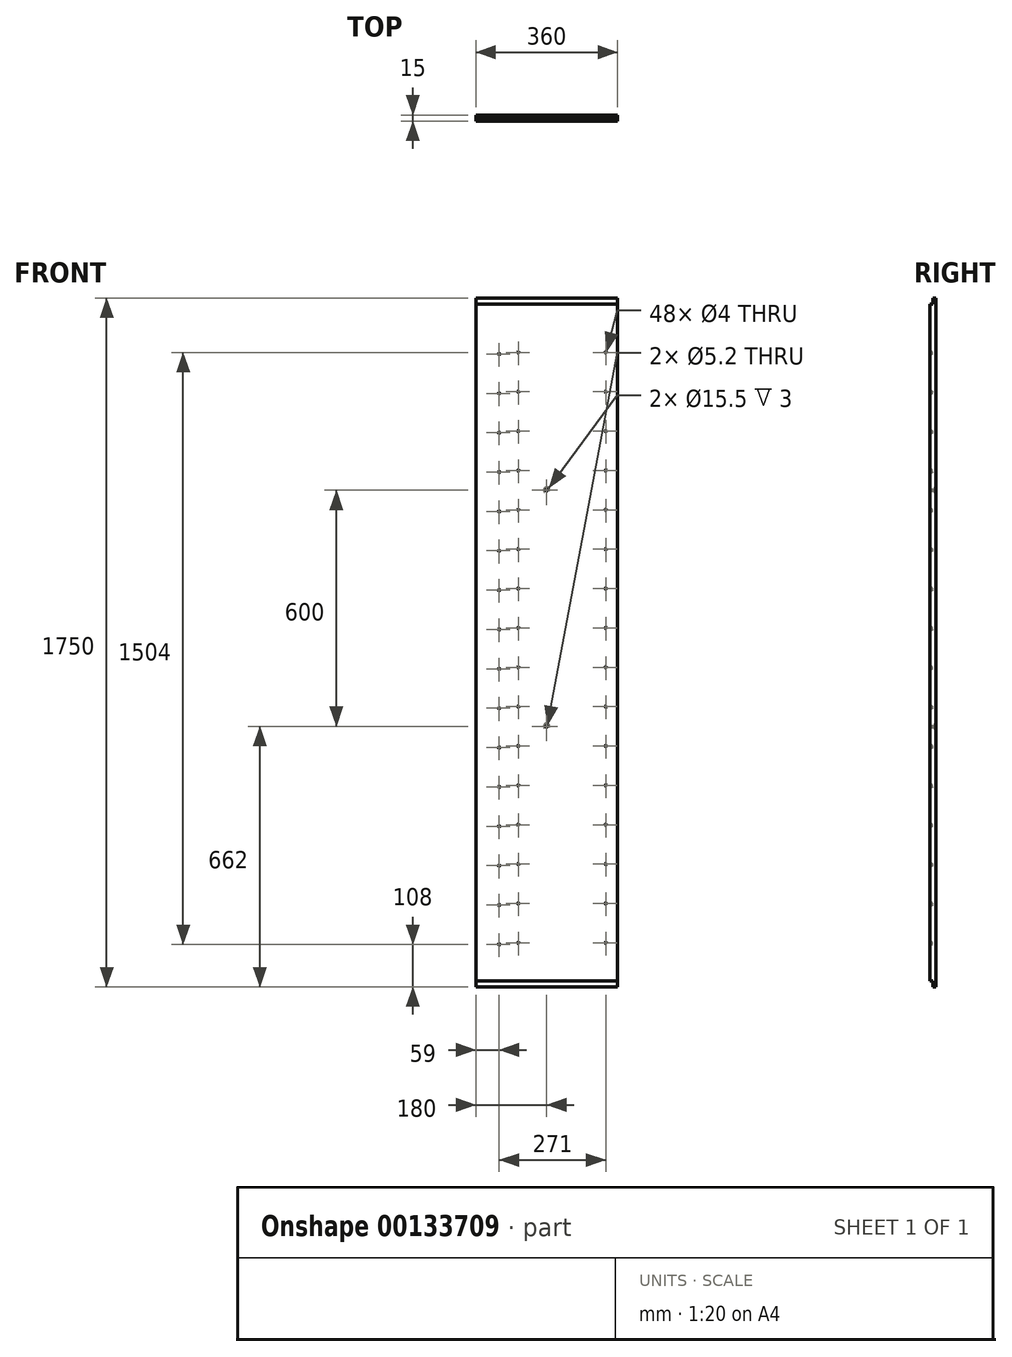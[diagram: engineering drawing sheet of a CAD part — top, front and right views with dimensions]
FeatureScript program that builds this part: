
annotation { "Feature Type Name" : "Feature", "Feature Type Description" : "" }
export const myFeature = defineFeature(function(context is Context, id is Id, definition is map)
    precondition{}
    {
        {
            var Q0;
            Q0=qCreatedBy(makeId("Front.planeOp"),FACE);
            var sketch = newSketch(context, id + "F0", { "sketchPlane" : qUnion([Q0])});
            skLineSegment(sketch, "E0.bottom", {"start": v(0, 0) * mm, "end": v(360, 0) * mm});
            skLineSegment(sketch, "E0.top", {"start": v(0, 1750) * mm, "end": v(360, 1750) * mm});
            skLineSegment(sketch, "E0.left", {"start": v(0, 0) * mm, "end": v(0, 1750) * mm});
            skLineSegment(sketch, "E0.right", {"start": v(360, 0) * mm, "end": v(360, 1750) * mm});
            skSolve(sketch);
        }
        {
            var Q0;
            Q0=makeQuery(id+"F0.imprint","IMPRINT",FACE,{"disambiguationData":[TD([[makeQuery(id+"F0.imprint","IMPRINT",EDGE,{"derivedFrom":sQuery(id+"F0.wireOp",EDGE,"E0.bottom")}),1.0]])]});
            extrude(context, id + "F1", {"entities" : qUnion([Q0]), "depth" : 15 * mm, "offsetDistance" : 25 * mm});
        }
        {
            var Q0;
            Q0=makeQuery(id+"F1.opExtrude","CAP_FACE",FACE,{"disambiguationData":[OSD([sQuery(id+"F0.wireOp",EDGE,"E0.bottom"),sQuery(id+"F0.wireOp",EDGE,"E0.top"),sQuery(id+"F0.wireOp",EDGE,"E0.left"),sQuery(id+"F0.wireOp",EDGE,"E0.right")])],"isStart":false});
            var sketch = newSketch(context, id + "F2", { "sketchPlane" : qUnion([Q0])});
            skPoint(sketch, "E1", {"position": v(330, 112) * mm});
            skPoint(sketch, "E2", {"position": v(108, 112) * mm});
            skPoint(sketch, "E3", {"position": v(59, 108) * mm});
            skPoint(sketch, "E4.0.1.0", {"position": v(59, 208) * mm});
            skPoint(sketch, "E4.0.1.1", {"position": v(108, 212) * mm});
            skPoint(sketch, "E4.0.1.2", {"position": v(330, 212) * mm});
            skPoint(sketch, "E4.0.2.0", {"position": v(59, 308) * mm});
            skPoint(sketch, "E4.0.2.1", {"position": v(108, 312) * mm});
            skPoint(sketch, "E4.0.2.2", {"position": v(330, 312) * mm});
            skPoint(sketch, "E4.0.3.0", {"position": v(59, 408) * mm});
            skPoint(sketch, "E4.0.3.1", {"position": v(108, 412) * mm});
            skPoint(sketch, "E4.0.3.2", {"position": v(330, 412) * mm});
            skPoint(sketch, "E4.0.4.0", {"position": v(59, 508) * mm});
            skPoint(sketch, "E4.0.4.1", {"position": v(108, 512) * mm});
            skPoint(sketch, "E4.0.4.2", {"position": v(330, 512) * mm});
            skPoint(sketch, "E4.0.5.0", {"position": v(59, 608) * mm});
            skPoint(sketch, "E4.0.5.1", {"position": v(108, 612) * mm});
            skPoint(sketch, "E4.0.5.2", {"position": v(330, 612) * mm});
            skPoint(sketch, "E4.0.6.0", {"position": v(59, 708) * mm});
            skPoint(sketch, "E4.0.6.1", {"position": v(108, 712) * mm});
            skPoint(sketch, "E4.0.6.2", {"position": v(330, 712) * mm});
            skPoint(sketch, "E4.0.7.0", {"position": v(59, 808) * mm});
            skPoint(sketch, "E4.0.7.1", {"position": v(108, 812) * mm});
            skPoint(sketch, "E4.0.7.2", {"position": v(330, 812) * mm});
            skPoint(sketch, "E4.0.8.0", {"position": v(59, 908) * mm});
            skPoint(sketch, "E4.0.8.1", {"position": v(108, 912) * mm});
            skPoint(sketch, "E4.0.8.2", {"position": v(330, 912) * mm});
            skPoint(sketch, "E4.0.9.0", {"position": v(59, 1008) * mm});
            skPoint(sketch, "E4.0.9.1", {"position": v(108, 1012) * mm});
            skPoint(sketch, "E4.0.9.2", {"position": v(330, 1012) * mm});
            skPoint(sketch, "E4.0.10.0", {"position": v(59, 1108) * mm});
            skPoint(sketch, "E4.0.10.1", {"position": v(108, 1112) * mm});
            skPoint(sketch, "E4.0.10.2", {"position": v(330, 1112) * mm});
            skPoint(sketch, "E4.0.11.0", {"position": v(59, 1208) * mm});
            skPoint(sketch, "E4.0.11.1", {"position": v(108, 1212) * mm});
            skPoint(sketch, "E4.0.11.2", {"position": v(330, 1212) * mm});
            skPoint(sketch, "E4.0.12.0", {"position": v(59, 1308) * mm});
            skPoint(sketch, "E4.0.12.1", {"position": v(108, 1312) * mm});
            skPoint(sketch, "E4.0.12.2", {"position": v(330, 1312) * mm});
            skPoint(sketch, "E4.0.13.0", {"position": v(59, 1408) * mm});
            skPoint(sketch, "E4.0.13.1", {"position": v(108, 1412) * mm});
            skPoint(sketch, "E4.0.13.2", {"position": v(330, 1412) * mm});
            skPoint(sketch, "E4.0.14.0", {"position": v(59, 1508) * mm});
            skPoint(sketch, "E4.0.14.1", {"position": v(108, 1512) * mm});
            skPoint(sketch, "E4.0.14.2", {"position": v(330, 1512) * mm});
            skPoint(sketch, "E4.0.15.0", {"position": v(59, 1608) * mm});
            skPoint(sketch, "E4.0.15.1", {"position": v(108, 1612) * mm});
            skPoint(sketch, "E4.0.15.2", {"position": v(330, 1612) * mm});
            skLineSegment(sketch, "E4.direction2", {"start": v(59, 108) * mm, "end": v(59, 208) * mm, "construction": true});
            skSolve(sketch);
        }
        {
            var Q0;
            Q0=sQuery(id+"F2.wireOp",VERTEX,"E4.0.12.0");
            var Q1;
            Q1=sQuery(id+"F2.wireOp",VERTEX,"E4.0.7.1");
            var Q2;
            Q2=sQuery(id+"F2.wireOp",VERTEX,"E4.0.12.2");
            var Q3;
            Q3=sQuery(id+"F2.wireOp",VERTEX,"E4.0.8.0");
            var Q4;
            Q4=sQuery(id+"F2.wireOp",VERTEX,"E4.0.13.2");
            var Q5;
            Q5=sQuery(id+"F2.wireOp",VERTEX,"E4.0.13.1");
            var Q6;
            Q6=sQuery(id+"F2.wireOp",VERTEX,"E4.0.9.0");
            var Q7;
            Q7=sQuery(id+"F2.wireOp",VERTEX,"E4.0.5.1");
            var Q8;
            Q8=sQuery(id+"F2.wireOp",VERTEX,"E4.0.5.0");
            var Q9;
            Q9=sQuery(id+"F2.wireOp",VERTEX,"E4.0.1.0");
            var Q10;
            Q10=sQuery(id+"F2.wireOp",VERTEX,"E4.0.2.0");
            var Q11;
            Q11=sQuery(id+"F2.wireOp",VERTEX,"E4.0.3.0");
            var Q12;
            Q12=sQuery(id+"F2.wireOp",VERTEX,"E4.0.14.2");
            var Q13;
            Q13=sQuery(id+"F2.wireOp",VERTEX,"E4.0.11.2");
            var Q14;
            Q14=sQuery(id+"F2.wireOp",VERTEX,"E4.0.7.0");
            var Q15;
            Q15=sQuery(id+"F2.wireOp",VERTEX,"E4.0.11.1");
            var Q16;
            Q16=sQuery(id+"F2.wireOp",VERTEX,"E4.0.15.2");
            var Q17;
            Q17=sQuery(id+"F2.wireOp",VERTEX,"E4.0.14.1");
            var Q18;
            Q18=sQuery(id+"F2.wireOp",VERTEX,"E4.0.10.1");
            var Q19;
            Q19=sQuery(id+"F2.wireOp",VERTEX,"E4.0.2.2");
            var Q20;
            Q20=sQuery(id+"F2.wireOp",VERTEX,"E4.0.2.1");
            var Q21;
            Q21=sQuery(id+"F2.wireOp",VERTEX,"E4.0.1.1");
            var Q22;
            Q22=sQuery(id+"F2.wireOp",VERTEX,"E4.0.4.1");
            var Q23;
            Q23=sQuery(id+"F2.wireOp",VERTEX,"E4.0.6.1");
            var Q24;
            Q24=sQuery(id+"F2.wireOp",VERTEX,"E4.0.5.2");
            var Q25;
            Q25=sQuery(id+"F2.wireOp",VERTEX,"E4.0.14.0");
            var Q26;
            Q26=sQuery(id+"F2.wireOp",VERTEX,"E4.0.12.1");
            var Q27;
            Q27=sQuery(id+"F2.wireOp",VERTEX,"E4.0.8.2");
            var Q28;
            Q28=sQuery(id+"F2.wireOp",VERTEX,"E4.0.15.0");
            var Q29;
            Q29=sQuery(id+"F2.wireOp",VERTEX,"E4.0.7.2");
            var Q30;
            Q30=sQuery(id+"F2.wireOp",VERTEX,"E4.0.9.2");
            var Q31;
            Q31=sQuery(id+"F2.wireOp",VERTEX,"E4.0.13.0");
            var Q32;
            Q32=sQuery(id+"F2.wireOp",VERTEX,"E4.0.1.2");
            var Q33;
            Q33=sQuery(id+"F2.wireOp",VERTEX,"E4.0.9.1");
            var Q34;
            Q34=sQuery(id+"F2.wireOp",VERTEX,"E4.direction1.end");
            var Q35;
            Q35=sQuery(id+"F2.wireOp",VERTEX,"E4.0.6.2");
            var Q36;
            Q36=sQuery(id+"F2.wireOp",VERTEX,"E2");
            var Q37;
            Q37=sQuery(id+"F2.wireOp",VERTEX,"E1");
            var Q38;
            Q38=sQuery(id+"F2.wireOp",VERTEX,"E4.0.4.2");
            var Q39;
            Q39=sQuery(id+"F2.wireOp",VERTEX,"E4.0.4.0");
            var Q40;
            Q40=sQuery(id+"F2.wireOp",VERTEX,"E3");
            var Q41;
            Q41=sQuery(id+"F2.wireOp",VERTEX,"E4.0.10.0");
            var Q42;
            Q42=sQuery(id+"F2.wireOp",VERTEX,"E4.0.15.1");
            var Q43;
            Q43=sQuery(id+"F2.wireOp",VERTEX,"E4.0.11.0");
            var Q44;
            Q44=sQuery(id+"F2.wireOp",VERTEX,"E4.0.6.0");
            var Q45;
            Q45=sQuery(id+"F2.wireOp",VERTEX,"E4.0.3.2");
            var Q46;
            Q46=sQuery(id+"F2.wireOp",VERTEX,"E4.0.3.1");
            var Q47;
            Q47=sQuery(id+"F2.wireOp",VERTEX,"E4.0.8.1");
            var Q48;
            Q48=sQuery(id+"F2.wireOp",VERTEX,"E4.0.10.2");
            var Q49;
            Q49=makeQuery(id+"F1.opExtrude","SWEPT_BODY",BODY,{"disambiguationData":[OSD([sQuery(id+"F0.wireOp",EDGE,"E0.bottom"),sQuery(id+"F0.wireOp",EDGE,"E0.top"),sQuery(id+"F0.wireOp",EDGE,"E0.left"),sQuery(id+"F0.wireOp",EDGE,"E0.right")])]});
            hole(context, id + "F3", {"style" : HoleStyle.SIMPLE, "endStyle" : HoleEndStyle.BLIND, "holeDiameter" : 4 * mm, "holeDepth" : 5 * mm, "isTappedThrough" : true, "tappedDepth" : 12 * mm, "tapClearance" : 3, "startFromSketch" : true, "locations" : qUnion([Q0, Q1, Q2, Q3, Q4, Q5, Q6, Q7, Q8, Q9, Q10, Q11, Q12, Q13, Q14, Q15, Q16, Q17, Q18, Q19, Q20, Q21, Q22, Q23, Q24, Q25, Q26, Q27, Q28, Q29, Q30, Q31, Q32, Q33, Q34, Q35, Q36, Q37, Q38, Q39, Q40, Q41, Q42, Q43, Q44, Q45, Q46, Q47, Q48]), "scope" : qUnion([Q49])});
        }
        {
            var Q0;
            Q0=makeQuery(id+"F1.opExtrude","CAP_FACE",FACE,{"disambiguationData":[OSD([sQuery(id+"F0.wireOp",EDGE,"E0.bottom"),sQuery(id+"F0.wireOp",EDGE,"E0.top"),sQuery(id+"F0.wireOp",EDGE,"E0.left"),sQuery(id+"F0.wireOp",EDGE,"E0.right")])],"isStart":true});
            var sketch = newSketch(context, id + "F4", { "sketchPlane" : qUnion([Q0])});
            skPoint(sketch, "E5.positionSnap0", {"position": v(-180, 0) * mm});
            skPoint(sketch, "E6", {"position": v(-180, 662) * mm});
            skPoint(sketch, "E7", {"position": v(-180, 1262) * mm});
            skSolve(sketch);
        }
        {
            var Q0;
            Q0=sQuery(id+"F4.wireOp",VERTEX,"E7");
            var Q1;
            Q1=sQuery(id+"F4.wireOp",VERTEX,"E6");
            var Q2;
            Q2=makeQuery(id+"F1.opExtrude","SWEPT_BODY",BODY,{"disambiguationData":[OSD([sQuery(id+"F0.wireOp",EDGE,"E0.bottom"),sQuery(id+"F0.wireOp",EDGE,"E0.top"),sQuery(id+"F0.wireOp",EDGE,"E0.left"),sQuery(id+"F0.wireOp",EDGE,"E0.right")])]});
            hole(context, id + "F5", {"style" : HoleStyle.C_BORE, "endStyle" : HoleEndStyle.BLIND, "holeDiameter" : 5.2 * mm, "cBoreDiameter" : 15.5 * mm, "cBoreDepth" : 3 * mm, "holeDepth" : 15 * mm, "isTappedThrough" : true, "tappedDepth" : 12 * mm, "tapClearance" : 3, "startFromSketch" : true, "locations" : qUnion([Q0, Q1]), "scope" : qUnion([Q2])});
        }
        {
            var Q0;
            Q0=makeQuery(id+"F1.opExtrude","SWEPT_FACE",FACE,{"disambiguationData":[OSD([sQuery(id+"F0.wireOp",EDGE,"E0.left")])]});
            var sketch = newSketch(context, id + "F6", { "sketchPlane" : qUnion([Q0])});
            skText(sketch, "E8", { "text": "123", "fontName": "OpenSans-Regular.ttf"});
            const initialGuessF6  = {"E8": [0, 0.8875, 1, 0, 0.00627]};
            skSetInitialGuess(sketch, initialGuessF6);
            skSolve(sketch);
        }
        {
            var Q0;
            Q0=makeQuery(id+"F6.imprint","IMPRINT",FACE,{"disambiguationData":[TD([[makeQuery(id+"F6.imprint","IMPRINT",EDGE,{"derivedFrom":sQuery(id+"F6.wireOp",EDGE,"E8.sketch_text.stroke-0")}),1.0]])]});
            var sketch = newSketch(context, id + "F7", { "sketchPlane" : qUnion([Q0])});
            skPoint(sketch, "E9.0", {"position": v(15, 0) * mm});
            skLineSegment(sketch, "E10.bottom", {"start": v(15, 0) * mm, "end": v(7.5, 0) * mm});
            skLineSegment(sketch, "E10.top", {"start": v(15, 15) * mm, "end": v(7.5, 15) * mm});
            skLineSegment(sketch, "E10.left", {"start": v(15, 0) * mm, "end": v(15, 15) * mm});
            skLineSegment(sketch, "E10.right", {"start": v(7.5, 0) * mm, "end": v(7.5, 15) * mm});
            skPoint(sketch, "E11.0", {"position": v(15, 1750) * mm});
            skLineSegment(sketch, "E12.bottom", {"start": v(15, 1750) * mm, "end": v(7.5, 1750) * mm});
            skLineSegment(sketch, "E12.top", {"start": v(15, 1735) * mm, "end": v(7.5, 1735) * mm});
            skLineSegment(sketch, "E12.left", {"start": v(15, 1750) * mm, "end": v(15, 1735) * mm});
            skLineSegment(sketch, "E12.right", {"start": v(7.5, 1750) * mm, "end": v(7.5, 1735) * mm});
            skSolve(sketch);
        }
        {
            var Q0;
            Q0 = qSketchRegion(id + "F7", true);
            extrude(context, id + "F8", {"entities" : qUnion([Q0]), "operationType" : NewBodyOperationType.REMOVE, "endBound" : BoundingType.UP_TO_NEXT, "oppositeDirection" : true, "depth" : 25 * mm, "offsetDistance" : 25 * mm});
        }
    });
